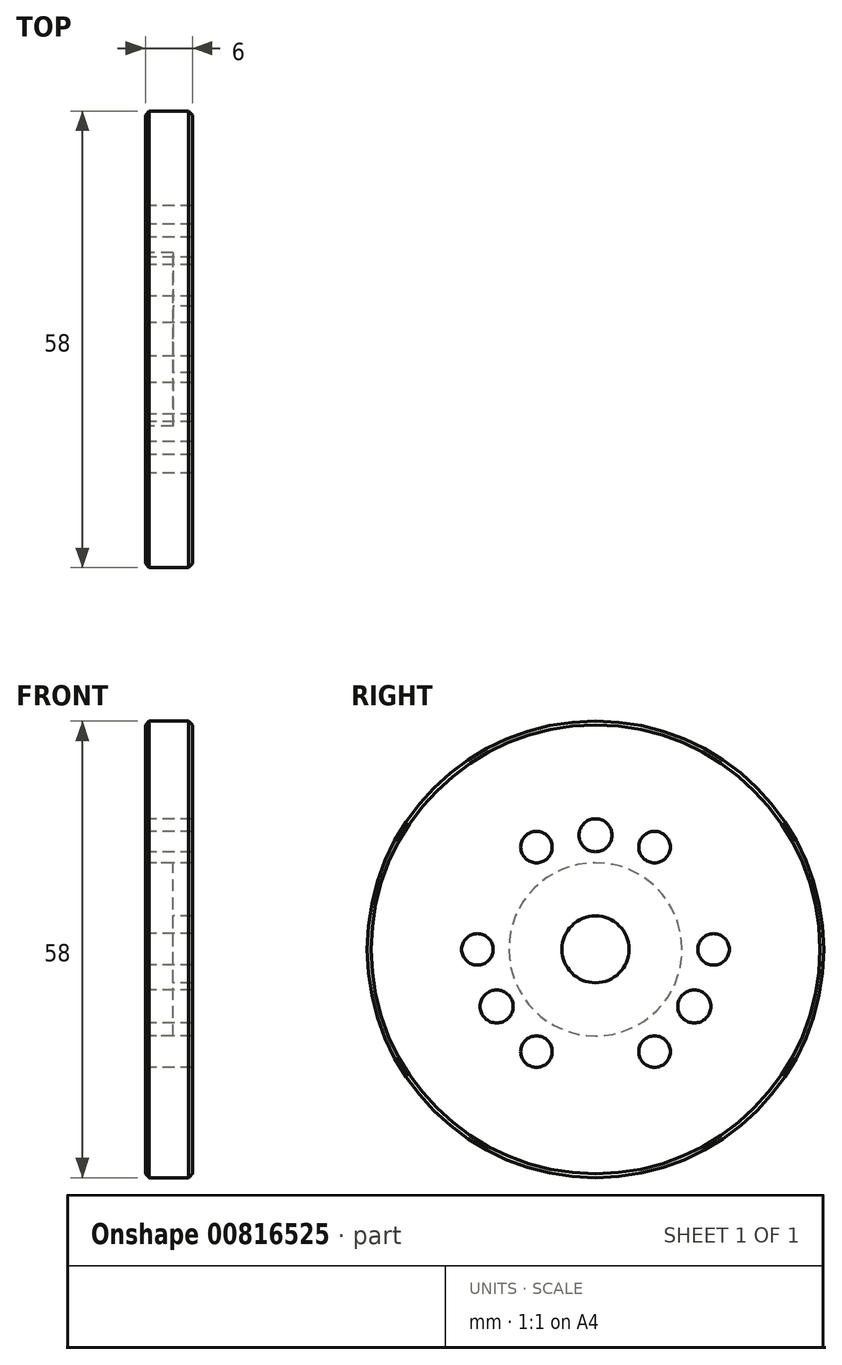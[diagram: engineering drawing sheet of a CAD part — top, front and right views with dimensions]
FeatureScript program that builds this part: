
annotation { "Feature Type Name" : "Feature", "Feature Type Description" : "" }
export const myFeature = defineFeature(function(context is Context, id is Id, definition is map)
    precondition{}
    {
        {
            var Q0;
            Q0=qCreatedBy(makeId("Right.planeOp"),FACE);
            var sketch = newSketch(context, id + "F0", { "sketchPlane" : qUnion([Q0])});
            skCircle(sketch, "E0", {"center": v(0, 0) * mm, "radius": 29 * mm});
            skCircle(sketch, "E1", {"center": v(0, 0) * mm, "radius": 14.5 * mm, "construction": true});
            skLineSegment(sketch, "E2", {"start": v(0, 65.04) * mm, "end": v(0, -65.63) * mm, "construction": true});
            skLineSegment(sketch, "E3", {"start": v(-69.13, 0) * mm, "end": v(64.07, 0) * mm, "construction": true});
            skLineSegment(sketch, "E4", {"start": v(0, 0) * mm, "end": v(56.85, -32.82) * mm, "construction": true});
            skLineSegment(sketch, "E5", {"start": v(0, 0) * mm, "end": v(29.3, -50.75) * mm, "construction": true});
            skLineSegment(sketch, "E6.MirrorCS", {"start": v(0, 0) * mm, "end": v(56.85, 32.82) * mm, "construction": true});
            skLineSegment(sketch, "E7.MirrorCS", {"start": v(0, 0) * mm, "end": v(29.3, 50.75) * mm, "construction": true});
            skLineSegment(sketch, "E8.MirrorCS", {"start": v(0, 0) * mm, "end": v(-29.3, 50.75) * mm, "construction": true});
            skLineSegment(sketch, "E9.MirrorCS", {"start": v(0, 0) * mm, "end": v(-56.85, 32.82) * mm, "construction": true});
            skLineSegment(sketch, "E10.MirrorCS", {"start": v(0, 0) * mm, "end": v(-56.85, -32.82) * mm, "construction": true});
            skLineSegment(sketch, "E11.MirrorCS", {"start": v(0, 0) * mm, "end": v(-29.3, -50.75) * mm, "construction": true});
            skCircle(sketch, "E12", {"center": v(0, 14.5) * mm, "radius": 2.1 * mm});
            skCircle(sketch, "E13", {"center": v(-12.56, -7.25) * mm, "radius": 2.1 * mm});
            skCircle(sketch, "E14", {"center": v(12.56, -7.25) * mm, "radius": 2.1 * mm});
            skCircle(sketch, "E15", {"center": v(0, 0) * mm, "radius": 15 * mm, "construction": true});
            skCircle(sketch, "E16", {"center": v(-7.5, -13) * mm, "radius": 2 * mm});
            skCircle(sketch, "E17", {"center": v(7.5, -13) * mm, "radius": 2 * mm});
            skCircle(sketch, "E18", {"center": v(15, 0) * mm, "radius": 2 * mm});
            skCircle(sketch, "E19", {"center": v(-15, 0) * mm, "radius": 2 * mm});
            skCircle(sketch, "E20", {"center": v(-7.5, 13) * mm, "radius": 2 * mm});
            skCircle(sketch, "E21", {"center": v(7.5, 13) * mm, "radius": 2 * mm});
            skCircle(sketch, "E22", {"center": v(0, 0) * mm, "radius": 4.25 * mm});
            skSolve(sketch);
        }
        {
            var Q0;
            Q0 = qSketchRegion(id + "F0", true);
            var Q1;
            Q1 = qSketchRegion(id + "F2", true);
            extrude(context, id + "F1", {"entities" : qUnion([Q0, Q1]), "depth" : 6 * mm, "offsetDistance" : 25 * mm});
        }
        {
            var Q0;
            Q0=qCreatedBy(makeId("Right.planeOp"),FACE);
            var sketch = newSketch(context, id + "F2", { "sketchPlane" : qUnion([Q0])});
            skCircle(sketch, "E23", {"center": v(0, 0) * mm, "radius": 11 * mm});
            skSolve(sketch);
        }
        {
            var Q0;
            Q0=makeQuery(id+"F2.imprint","IMPRINT",FACE,{"disambiguationData":[TD([[makeQuery(id+"F2.imprint","IMPRINT",EDGE,{"derivedFrom":sQuery(id+"F2.wireOp",EDGE,"E23")}),1.0]])]});
            extrude(context, id + "F3", {"entities" : qUnion([Q0]), "operationType" : NewBodyOperationType.REMOVE, "depth" : 3.5 * mm, "offsetDistance" : 25 * mm});
        }
        {
            var Q0;
            Q0=makeQuery(id+"F3.boolean.opBoolean","COPY",EDGE,{"derivedFrom":makeQuery(id+"F3.opExtrude","CAP_EDGE",EDGE,{"disambiguationData":[OSD([sQuery(id+"F2.wireOp",EDGE,"E23")])],"isStart":true})});
            var Q1;
            Q1=makeQuery(id+"F1.opExtrude","CAP_EDGE",EDGE,{"disambiguationData":[OSD([sQuery(id+"F0.wireOp",EDGE,"E0")])],"isStart":true});
            var Q2;
            Q2=makeQuery(id+"F1.opExtrude","CAP_EDGE",EDGE,{"disambiguationData":[OSD([sQuery(id+"F0.wireOp",EDGE,"E0")])],"isStart":false});
            chamfer(context, id + "F4", {"entities" : qUnion([Q0, Q1, Q2]), "width" : 0.5 * mm, "tangentPropagation" : true});
        }
    });
